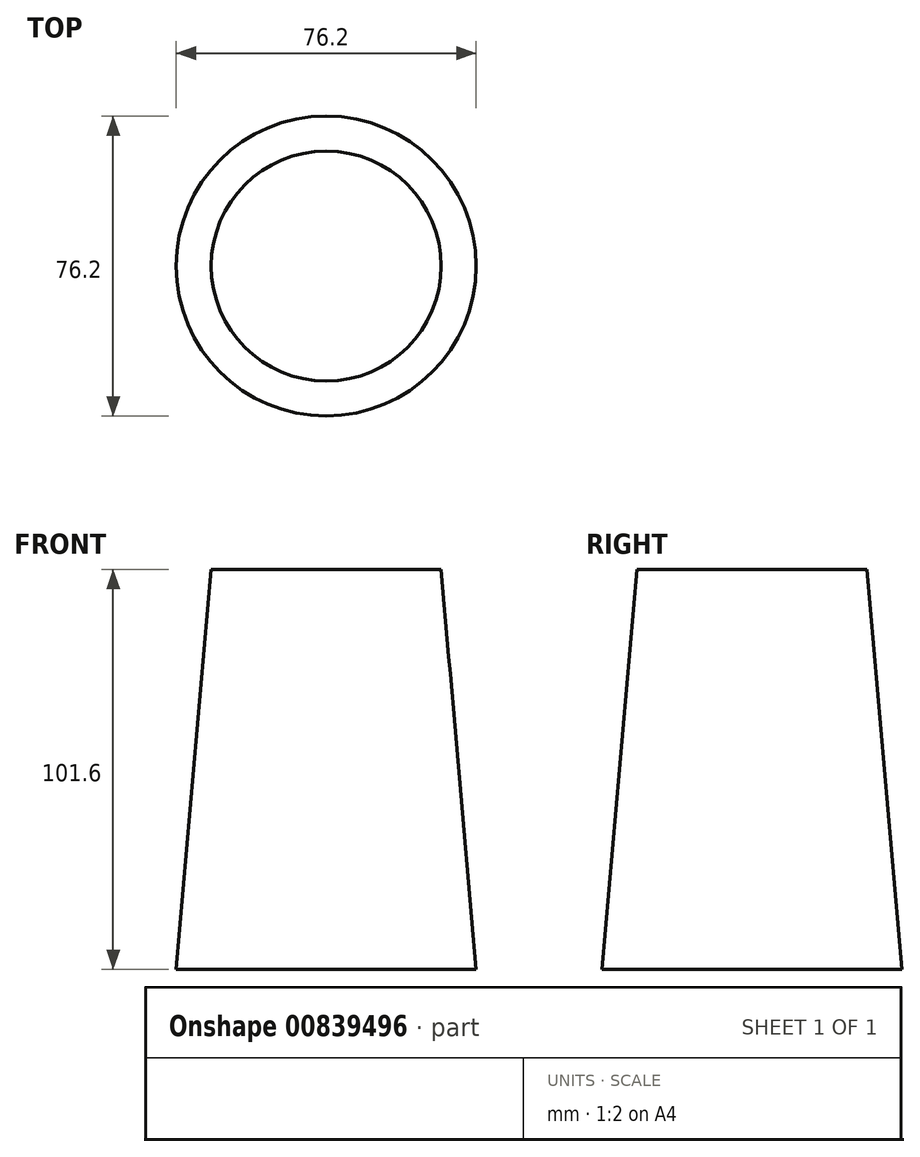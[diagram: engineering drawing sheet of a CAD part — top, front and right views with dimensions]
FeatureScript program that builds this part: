
annotation { "Feature Type Name" : "Feature", "Feature Type Description" : "" }
export const myFeature = defineFeature(function(context is Context, id is Id, definition is map)
    precondition{}
    {
        {
            var Q0;
            Q0=qCreatedBy(makeId("Top.planeOp"),FACE);
            var sketch = newSketch(context, id + "F0", { "sketchPlane" : qUnion([Q0])});
            skCircle(sketch, "E0", {"center": v(0, 0) * mm, "radius": 38.1 * mm});
            skSolve(sketch);
        }
        {
            var Q0;
            Q0 = qSketchRegion(id + "F0", true);
            extrude(context, id + "F1", {"entities" : qUnion([Q0]), "depth" : 101.6 * mm, "offsetDistance" : 25.4 * mm, "hasDraft" : true, "draftAngle" : 5 * degree, "draftPullDirection" : true});
        }
    });
